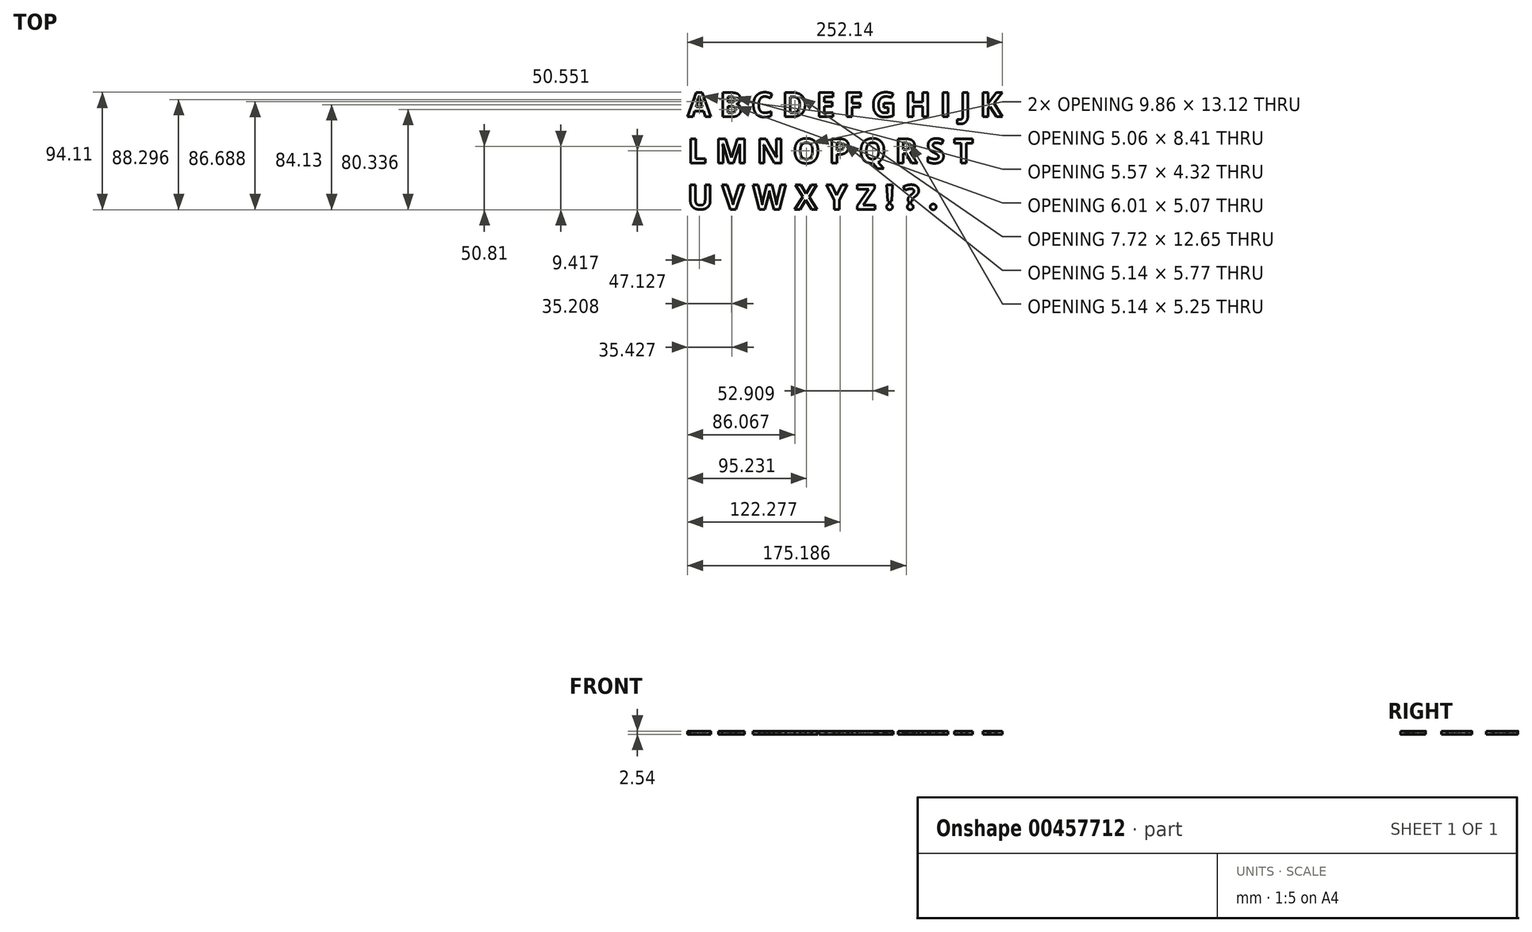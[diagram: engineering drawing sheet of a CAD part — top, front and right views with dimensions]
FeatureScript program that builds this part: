
annotation { "Feature Type Name" : "Feature", "Feature Type Description" : "" }
export const myFeature = defineFeature(function(context is Context, id is Id, definition is map)
    precondition{}
    {
        {
            var Q0;
            Q0=qCreatedBy(makeId("Top.planeOp"),FACE);
            var sketch = newSketch(context, id + "F0", { "sketchPlane" : qUnion([Q0])});
            skText(sketch, "E0", { "text": "A B C D E F G H I J K\nL M N O P Q R S T\nU V W X Y Z ! ? .", "fontName": "OpenSans-Bold.ttf"});
            skLineSegment(sketch, "E1", {"start": v(43.98, -67.54) * mm, "end": v(43.98, -70.11) * mm});
            skLineSegment(sketch, "E2", {"start": v(44.93, -67.3) * mm, "end": v(44.93, -70.7) * mm});
            skLineSegment(sketch, "E3", {"start": v(59.9, -67.23) * mm, "end": v(59.9, -71.02) * mm});
            skLineSegment(sketch, "E4", {"start": v(61.35, -66.69) * mm, "end": v(61.35, -71.02) * mm});
            const initialGuessF0  = {"E0": [-0.11735, 0, 1, 0, 0.0196]};
            skSetInitialGuess(sketch, initialGuessF0);
            skSolve(sketch);
        }
        {
            var Q0;
            Q0 = qSketchRegion(id + "F0", true);
            extrude(context, id + "F1", {"entities" : qUnion([Q0]), "depth" : 2.54 * mm});
        }
        {
            var Q0;
            {var subQ1=sQuery(id+"F0.wireOp",EDGE,"E0.sketch_text.stroke-395");var subQ5=sQuery(id+"F0.wireOp",EDGE,"E4");var subQ6=makeQuery(id+"F0.imprint","INTERSECT",VERTEX,{"derivedFrom":[subQ1,subQ5]});Q0=makeQuery(id+"F0.imprint","IMPRINT",FACE,{"disambiguationData":[TD([[makeQuery(id+"F0.imprint","IMPRINT",EDGE,{"disambiguationData":[TD([[subQ6,-1.0]])],"derivedFrom":subQ1}),1.0]])]});}
            extrude(context, id + "F2", {"entities" : qUnion([Q0]), "operationType" : NewBodyOperationType.ADD, "depth" : 2.54 * mm});
        }
    });
